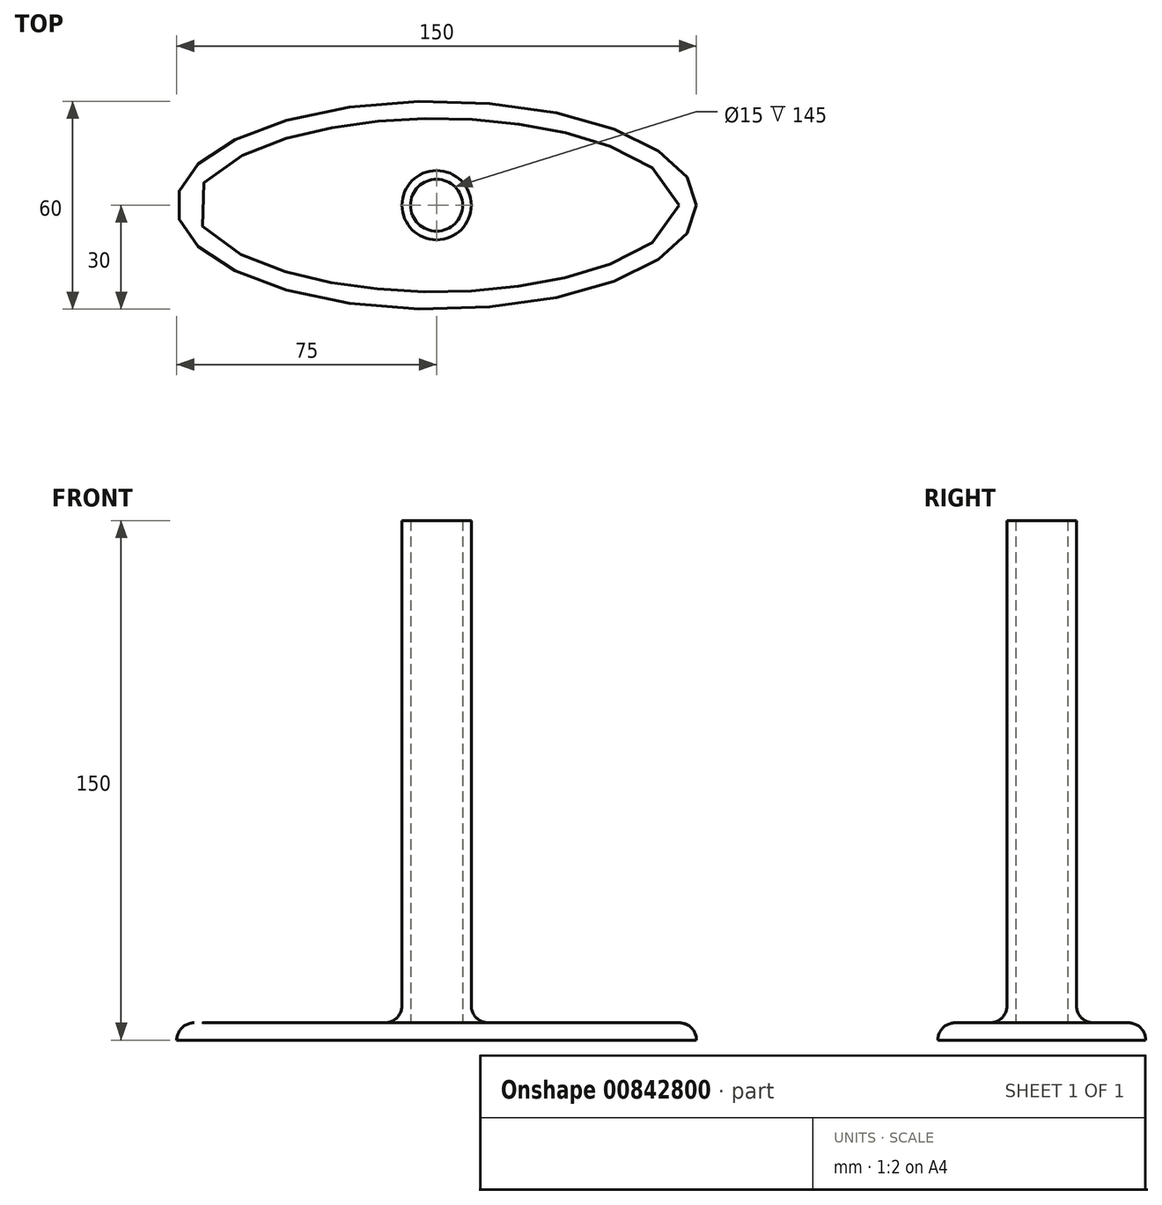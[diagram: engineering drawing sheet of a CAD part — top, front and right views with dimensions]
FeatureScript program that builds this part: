
annotation { "Feature Type Name" : "Feature", "Feature Type Description" : "" }
export const myFeature = defineFeature(function(context is Context, id is Id, definition is map)
    precondition{}
    {
        {
            var Q0;
            Q0=qCreatedBy(makeId("Top.planeOp"),FACE);
            var sketch = newSketch(context, id + "F0", { "sketchPlane" : qUnion([Q0])});
            skEllipse(sketch, "E0", {"center": v(0, 0) * mm, "majorRadius": 75 * mm, "minorRadius": 30 * mm, "majorAxis": v(1, 0)});
            skSolve(sketch);
        }
        {
            var Q0;
            Q0=qCreatedBy(makeId("Top.planeOp"),FACE);
            var sketch = newSketch(context, id + "F1", { "sketchPlane" : qUnion([Q0])});
            skCircle(sketch, "E1", {"center": v(0, 0) * mm, "radius": 10 * mm});
            skSolve(sketch);
        }
        {
            var Q0;
            Q0=makeQuery(id+"F1.imprint","IMPRINT",FACE,{"disambiguationData":[TD([[makeQuery(id+"F1.imprint","IMPRINT",EDGE,{"derivedFrom":sQuery(id+"F1.wireOp",EDGE,"E1")}),1.0]])]});
            extrude(context, id + "F2", {"entities" : qUnion([Q0]), "depth" : 150 * mm, "offsetDistance" : 25 * mm});
        }
        {
            var Q0;
            Q0=makeQuery(id+"F2.opExtrude","CAP_FACE",FACE,{"disambiguationData":[OSD([sQuery(id+"F1.wireOp",EDGE,"E1")])],"isStart":false});
            shell(context, id + "F3", {"entities" : qUnion([Q0]), "thickness" : 2.5 * mm});
        }
        {
            var Q0;
            Q0=makeQuery(id+"F0.imprint","IMPRINT",FACE,{"disambiguationData":[TD([[makeQuery(id+"F0.imprint","IMPRINT",EDGE,{"derivedFrom":sQuery(id+"F0.wireOp",EDGE,"E0")}),1.0]])]});
            extrude(context, id + "F4", {"entities" : qUnion([Q0]), "operationType" : NewBodyOperationType.ADD, "depth" : 5 * mm, "offsetDistance" : 25 * mm});
        }
        {
            var Q0;
            Q0=makeQuery(id+"F4.boolean.opBoolean","INTERSECT",EDGE,{"derivedFrom":[makeQuery(id+"F2.opExtrude","SWEPT_FACE",FACE,{"disambiguationData":[OSD([sQuery(id+"F1.wireOp",EDGE,"E1")])]}),makeQuery(id+"F4.opExtrude","CAP_FACE",FACE,{"disambiguationData":[OSD([sQuery(id+"F0.wireOp",EDGE,"E0")])],"isStart":false})]});
            var Q1;
            {var subQ0=sQuery(id+"F0.wireOp",EDGE,"E0");Q1=makeQuery(id+"F4.boolean.opBoolean","SPLIT",FACE,{"disambiguationData":[TD([makeQuery(id+"F2.opExtrude","SWEPT_FACE",FACE,{"disambiguationData":[OSD([sQuery(id+"F1.wireOp",EDGE,"E1")])]})])],"derivedFrom":makeQuery(id+"F4.opExtrude","CAP_FACE",FACE,{"disambiguationData":[OSD([subQ0])],"isStart":false})});}
            fillet(context, id + "F5", {"entities" : qUnion([Q0, Q1]), "radius" : 5 * mm, "tangentPropagation" : true, "allowEdgeOverflow" : false});
        }
    });
